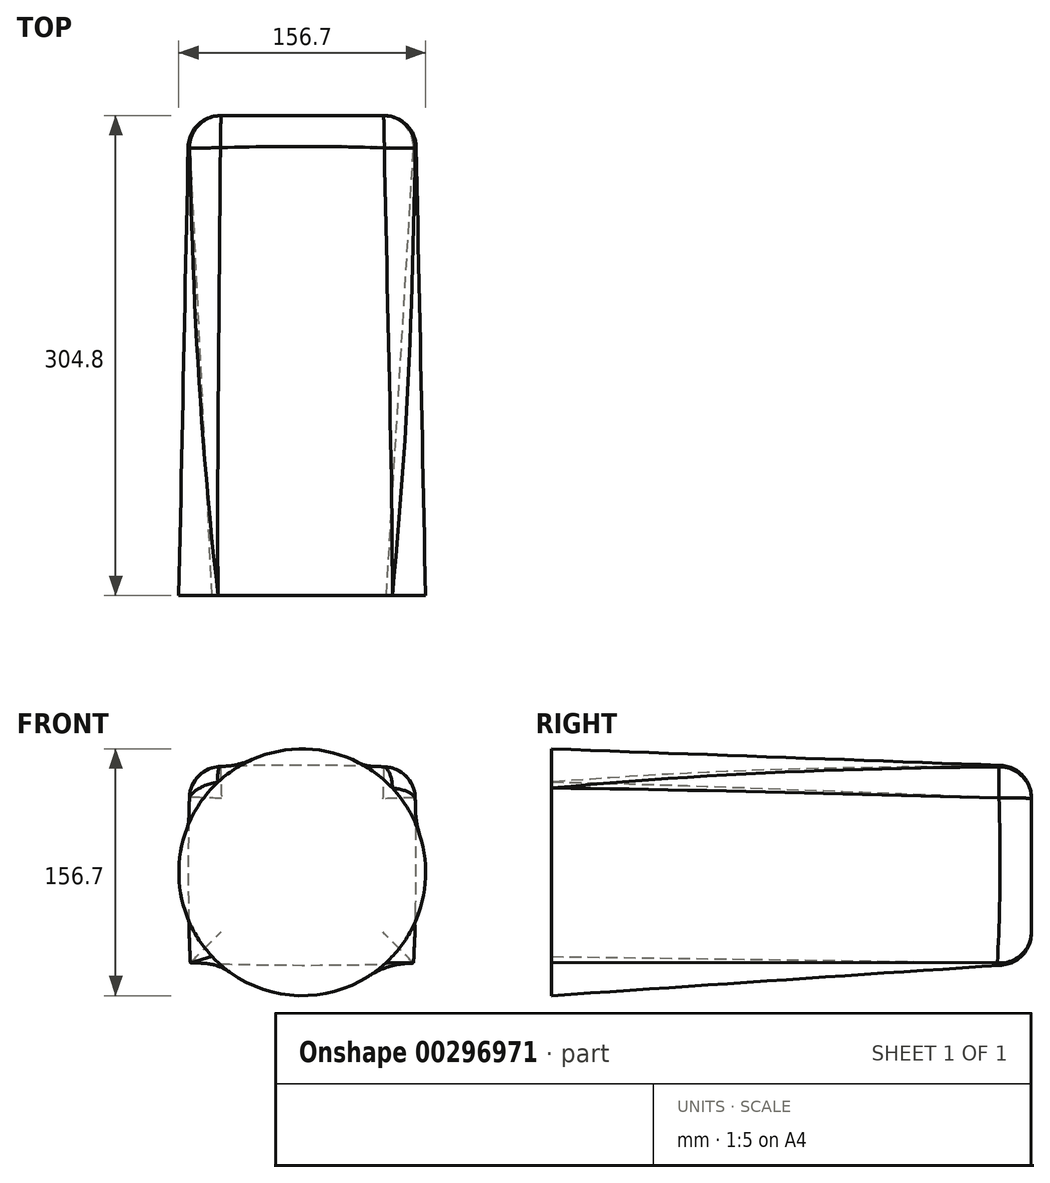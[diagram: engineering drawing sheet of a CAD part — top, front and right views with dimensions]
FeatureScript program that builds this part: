
annotation { "Feature Type Name" : "Feature", "Feature Type Description" : "" }
export const myFeature = defineFeature(function(context is Context, id is Id, definition is map)
    precondition{}
    {
        {
            var Q0;
            Q0=qCreatedBy(makeId("Front.planeOp"),FACE);
            var sketch = newSketch(context, id + "F0", { "sketchPlane" : qUnion([Q0])});
            skCircle(sketch, "E0", {"center": v(0, 0) * mm, "radius": 78.35 * mm});
            skSolve(sketch);
        }
        {
            var Q0;
            Q0=qCreatedBy(makeId("Front.planeOp"),FACE);
            cPlane(context, id + "F1", {"entities" : qUnion([Q0]), "cplaneType" : CPlaneType.OFFSET, "offset" : 304.8 * mm, "oppositeDirection" : true, "width" : 152.4 * mm, "height" : 152.4 * mm});
        }
        {
            var Q0;
            Q0=qCreatedBy(id+"F1.planeOp",FACE);
            var sketch = newSketch(context, id + "F2", { "sketchPlane" : qUnion([Q0])});
            skLineSegment(sketch, "E1.bottom", {"start": v(72.02, 67.24) * mm, "end": v(-72.02, 67.24) * mm});
            skLineSegment(sketch, "E1.top", {"start": v(72.02, -57.68) * mm, "end": v(-72.02, -57.68) * mm});
            skLineSegment(sketch, "E1.left", {"start": v(72.02, 67.24) * mm, "end": v(72.02, -57.68) * mm});
            skLineSegment(sketch, "E1.right", {"start": v(-72.02, 67.24) * mm, "end": v(-72.02, -57.68) * mm});
            skPoint(sketch, "E1.middle", {"position": v(0, 4.78) * mm});
            skSolve(sketch);
        }
        {
            var Q0;
            Q0 = qSketchRegion(id + "F0", true);
            var Q1;
            Q1 = qSketchRegion(id + "F2", true);
            loft(context, id + "F3", {"sheetProfilesArray" : [{ "sheetProfileEntities" : qUnion([Q0]) }, { "sheetProfileEntities" : qUnion([Q1]) }]});
        }
        {
            var Q0;
            Q0=makeQuery(id+"F3.opLoft","SWEPT_EDGE",EDGE,{"disambiguationData":[OSD([sQuery(id+"F0.wireOp",EDGE,"E0"),sQuery(id+"F2.wireOp",EDGE,"E1.bottom"),sQuery(id+"F2.wireOp",EDGE,"E1.top"),sQuery(id+"F2.wireOp",EDGE,"E1.left")])]});
            var Q1;
            Q1=makeQuery(id+"F3.opLoft","SWEPT_EDGE",EDGE,{"disambiguationData":[OSD([sQuery(id+"F2.wireOp",EDGE,"E1.bottom"),sQuery(id+"F2.wireOp",EDGE,"E1.left")])]});
            var Q2;
            Q2=makeQuery(id+"F3.opLoft","CAP_FACE",FACE,{"disambiguationData":[OSD([makeQuery(id+"F2.imprint","IMPRINT",FACE,{"disambiguationData":[TD([[makeQuery(id+"F2.imprint","IMPRINT",EDGE,{"derivedFrom":sQuery(id+"F2.wireOp",EDGE,"E1.bottom")}),1.0]])]})])],"isStart":true});
            fillet(context, id + "F4", {"entities" : qUnion([Q0, Q1, Q2]), "radius" : 20.32 * mm, "tangentPropagation" : true, "allowEdgeOverflow" : false});
        }
    });
